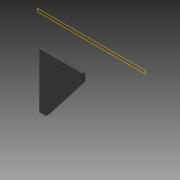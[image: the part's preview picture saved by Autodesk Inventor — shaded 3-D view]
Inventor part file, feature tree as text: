
AUTODESK INVENTOR PART (.ipt)
format: ipt  version: 2013 (Build 170138000, 138)  size: 111,616 bytes
history: native  units: in
note: dims shown in document units (in); Inventor stores cm internally (conversion verified against a paired STEP export)
features: sketch x3, extrude x2, reference x2, plane x1, hole x1
ambient origin geometry x8: Origin, YZ Plane, XZ Plane, XY Plane, X Axis, Y Axis, Z Axis, Center Point
bodies: Solid1 (feature_tree)
feature tree (9):
  plane  "Work Plane1"
  extrude  "Extrusion1"  Depth=0.4921in TaperAngle=0.0deg
  extrude  "Extrusion2"  Depth=1.0827in
  hole  "Hole1"  [1 undecoded]
  sketch  "Sketch1"  dims[d2=9.8425in d3=0.4921in d4=0.0in]
  reference  "Reference1"
  reference  "Reference2"
  sketch  "Sketch2"  dims[d5=0.7874in d6=1.0827in]
  sketch  "Sketch3"  dims[d7=1.0in d8=0.0in d9=0.134in d10=0.75in d11=0.256in d12=0.118in d13=0.5635in d14=1.0in d15=0.8108in]
note: 1 required parameter value undecoded (feature->parameter linkage not recoverable at this tier; creation-order binding heuristic only, values carry confidence <= 0.55)
